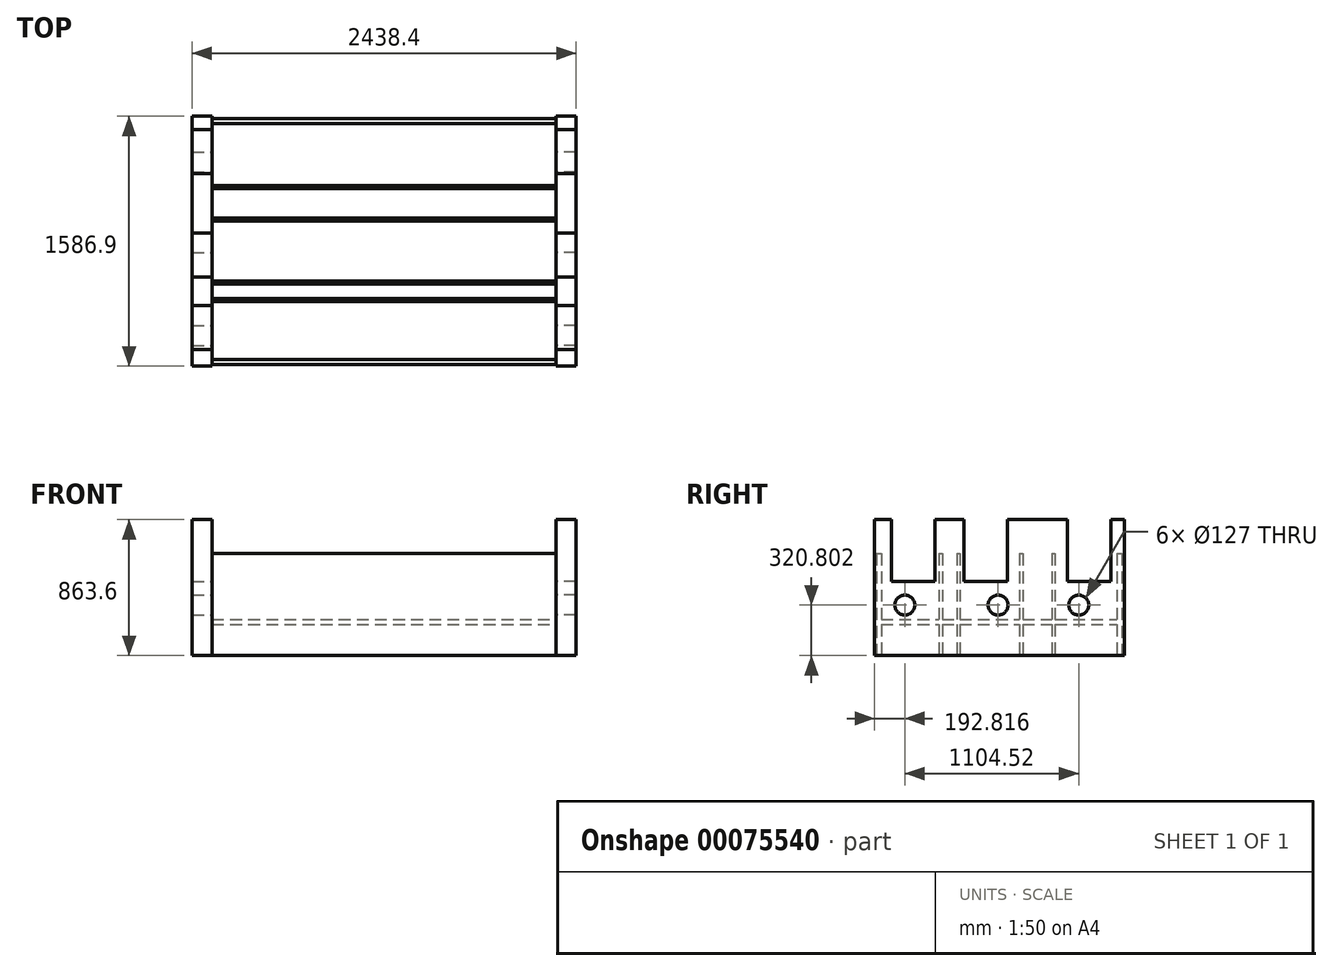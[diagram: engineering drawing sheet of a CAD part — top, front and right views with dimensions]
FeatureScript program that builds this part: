
annotation { "Feature Type Name" : "Feature", "Feature Type Description" : "" }
export const myFeature = defineFeature(function(context is Context, id is Id, definition is map)
    precondition{}
    {
        {
            var Q0;
            Q0=qCreatedBy(makeId("Right.planeOp"),FACE);
            var sketch = newSketch(context, id + "F0", { "sketchPlane" : qUnion([Q0])});
            skLineSegment(sketch, "E0", {"start": v(-793.45, 0) * mm, "end": v(793.45, 0) * mm});
            skLineSegment(sketch, "E1.0", {"start": v(-793.45, 863.6) * mm, "end": v(-686.92, 863.6) * mm});
            skLineSegment(sketch, "E2", {"start": v(-793.45, 0) * mm, "end": v(-793.45, 863.6) * mm});
            skLineSegment(sketch, "E3", {"start": v(793.45, 0) * mm, "end": v(793.45, 863.6) * mm});
            skLineSegment(sketch, "E4.0", {"start": v(-408.28, 0) * mm, "end": v(-408.28, 863.6) * mm, "construction": true});
            skLineSegment(sketch, "E5.0", {"start": v(-686.92, 0) * mm, "end": v(-686.92, 863.6) * mm, "construction": true});
            skLineSegment(sketch, "E6.0", {"start": v(52.1, 0) * mm, "end": v(52.1, 863.6) * mm, "construction": true});
            skLineSegment(sketch, "E7.0", {"start": v(-226.54, 0) * mm, "end": v(-226.54, 863.6) * mm, "construction": true});
            skLineSegment(sketch, "E8.0", {"start": v(709.12, 0) * mm, "end": v(709.12, 939.8) * mm, "construction": true});
            skLineSegment(sketch, "E9.0", {"start": v(430.48, 0) * mm, "end": v(430.48, 863.6) * mm, "construction": true});
            skLineSegment(sketch, "E10.top", {"start": v(-686.92, 469.9) * mm, "end": v(-408.28, 469.9) * mm});
            skLineSegment(sketch, "E10.left", {"start": v(-686.92, 863.6) * mm, "end": v(-686.92, 469.9) * mm});
            skLineSegment(sketch, "E10.right", {"start": v(-408.28, 863.6) * mm, "end": v(-408.28, 469.9) * mm});
            skLineSegment(sketch, "E11.top", {"start": v(-226.54, 469.9) * mm, "end": v(52.1, 469.9) * mm});
            skLineSegment(sketch, "E11.left", {"start": v(-226.54, 863.6) * mm, "end": v(-226.54, 469.9) * mm});
            skLineSegment(sketch, "E11.right", {"start": v(52.1, 863.6) * mm, "end": v(52.1, 469.9) * mm});
            skLineSegment(sketch, "E12.top", {"start": v(430.48, 469.9) * mm, "end": v(709.12, 469.9) * mm});
            skLineSegment(sketch, "E12.left", {"start": v(430.48, 863.6) * mm, "end": v(430.48, 469.9) * mm});
            skLineSegment(sketch, "E12.right", {"start": v(709.12, 863.6) * mm, "end": v(709.12, 469.9) * mm});
            skLineSegment(sketch, "E13.trimOffspring", {"start": v(-408.28, 863.6) * mm, "end": v(-226.54, 863.6) * mm});
            skLineSegment(sketch, "E14.trimOffspring", {"start": v(52.1, 863.6) * mm, "end": v(430.48, 863.6) * mm});
            skLineSegment(sketch, "E15.trimOffspring", {"start": v(709.12, 863.6) * mm, "end": v(793.45, 863.6) * mm});
            skLineSegment(sketch, "E16.0", {"start": v(503.89, -556.3) * mm, "end": v(503.89, 863.6) * mm, "construction": true});
            skLineSegment(sketch, "E17.0", {"start": v(-8.3, -556.3) * mm, "end": v(-8.3, 863.6) * mm, "construction": true});
            skLineSegment(sketch, "E18.0", {"start": v(-600.63, -556.3) * mm, "end": v(-600.63, 863.6) * mm, "construction": true});
            skLineSegment(sketch, "E19", {"start": v(793.45, 863.6) * mm, "end": v(-1048.26, 863.6) * mm, "construction": true});
            skLineSegment(sketch, "E20.0", {"start": v(793.45, 244.6) * mm, "end": v(-1048.26, 244.6) * mm, "construction": true});
            skLineSegment(sketch, "E21.0", {"start": v(793.45, 320.8) * mm, "end": v(-1048.26, 320.8) * mm, "construction": true});
            skCircle(sketch, "E22", {"center": v(-600.63, 320.8) * mm, "radius": 63.5 * mm});
            skCircle(sketch, "E23", {"center": v(-8.3, 320.8) * mm, "radius": 63.5 * mm});
            skCircle(sketch, "E24", {"center": v(503.89, 320.8) * mm, "radius": 63.5 * mm});
            skSolve(sketch);
        }
        {
            var Q0;
            Q0 = qSketchRegion(id + "F0", true);
            extrude(context, id + "F1", {"entities" : qUnion([Q0]), "depth" : 127 * mm});
        }
        {
            var Q0;
            Q0=makeQuery(id+"F0.imprint","IMPRINT",FACE,{"disambiguationData":[TD([[makeQuery(id+"F0.imprint","IMPRINT",EDGE,{"derivedFrom":sQuery(id+"F0.wireOp",EDGE,"E0")}),1.0]])]});
            var sketch = newSketch(context, id + "F2", { "sketchPlane" : qUnion([Q0])});
            skLineSegment(sketch, "E25.0", {"start": v(430.48, 469.9) * mm, "end": v(709.12, 469.9) * mm, "construction": true});
            skLineSegment(sketch, "E26.0", {"start": v(-226.54, 469.9) * mm, "end": v(52.1, 469.9) * mm, "construction": true});
            skLineSegment(sketch, "E27.0", {"start": v(-686.92, 469.9) * mm, "end": v(-408.28, 469.9) * mm, "construction": true});
            skLineSegment(sketch, "E28.0", {"start": v(709.12, 863.6) * mm, "end": v(709.12, 469.9) * mm, "construction": true});
            skLineSegment(sketch, "E29.0", {"start": v(430.48, 863.6) * mm, "end": v(430.48, 469.9) * mm, "construction": true});
            skLineSegment(sketch, "E30.0", {"start": v(709.12, 863.6) * mm, "end": v(793.45, 863.6) * mm, "construction": true});
            skLineSegment(sketch, "E31.0", {"start": v(52.1, 863.6) * mm, "end": v(430.48, 863.6) * mm, "construction": true});
            skLineSegment(sketch, "E32.0", {"start": v(52.1, 863.6) * mm, "end": v(52.1, 469.9) * mm, "construction": true});
            skLineSegment(sketch, "E33.0", {"start": v(-226.54, 863.6) * mm, "end": v(-226.54, 469.9) * mm, "construction": true});
            skLineSegment(sketch, "E34.0", {"start": v(-408.28, 863.6) * mm, "end": v(-226.54, 863.6) * mm, "construction": true});
            skLineSegment(sketch, "E35.0", {"start": v(-408.28, 863.6) * mm, "end": v(-408.28, 469.9) * mm, "construction": true});
            skLineSegment(sketch, "E36.0", {"start": v(-686.92, 863.6) * mm, "end": v(-686.92, 469.9) * mm, "construction": true});
            skLineSegment(sketch, "E37.0", {"start": v(-793.45, 863.6) * mm, "end": v(-686.92, 863.6) * mm, "construction": true});
            skLineSegment(sketch, "E38.0", {"start": v(-793.45, 0) * mm, "end": v(-793.45, 863.6) * mm, "construction": true});
            skLineSegment(sketch, "E39.0", {"start": v(-793.45, 0) * mm, "end": v(793.45, 0) * mm, "construction": true});
            skLineSegment(sketch, "E40.0", {"start": v(793.45, 0) * mm, "end": v(793.45, 863.6) * mm, "construction": true});
            skCircle(sketch, "E41.0", {"center": v(503.89, 320.8) * mm, "radius": 63.5 * mm, "construction": true});
            skCircle(sketch, "E42.0", {"center": v(-8.3, 320.8) * mm, "radius": 63.5 * mm, "construction": true});
            skCircle(sketch, "E43.0", {"center": v(-600.63, 320.8) * mm, "radius": 63.5 * mm, "construction": true});
            skLineSegment(sketch, "E44.0", {"start": v(793.45, 244.6) * mm, "end": v(-1048.26, 244.6) * mm, "construction": true});
            skLineSegment(sketch, "E45", {"start": v(569.8, 469.9) * mm, "end": v(569.8, -392.27) * mm, "construction": true});
            skLineSegment(sketch, "E46", {"start": v(-87.22, 469.9) * mm, "end": v(-87.22, -400.88) * mm, "construction": true});
            skLineSegment(sketch, "E47", {"start": v(-547.6, 469.9) * mm, "end": v(-547.6, -378.83) * mm, "construction": true});
            skLineSegment(sketch, "E48.0", {"start": v(-782.55, 647.7) * mm, "end": v(-750.8, 647.7) * mm});
            skLineSegment(sketch, "E49.0", {"start": v(-382.5, 647.7) * mm, "end": v(-382.5, 0) * mm});
            skLineSegment(sketch, "E50.0", {"start": v(-750.8, 647.7) * mm, "end": v(-750.8, 0) * mm});
            skLineSegment(sketch, "E51.0", {"start": v(-782.55, 647.7) * mm, "end": v(-782.55, 0) * mm});
            skLineSegment(sketch, "E52.0", {"start": v(-363.45, 647.7) * mm, "end": v(-363.45, 0) * mm});
            skLineSegment(sketch, "E53.0", {"start": v(128.68, 647.7) * mm, "end": v(128.68, 0) * mm});
            skLineSegment(sketch, "E54.0", {"start": v(147.73, 647.7) * mm, "end": v(147.73, 0) * mm});
            skLineSegment(sketch, "E55.0", {"start": v(-252.32, 647.7) * mm, "end": v(-252.32, 0) * mm});
            skLineSegment(sketch, "E56.0", {"start": v(-271.37, 647.7) * mm, "end": v(-271.37, 0) * mm});
            skLineSegment(sketch, "E57.0", {"start": v(747.6, 647.7) * mm, "end": v(747.6, 0) * mm});
            skLineSegment(sketch, "E58.0", {"start": v(779.35, 647.7) * mm, "end": v(779.35, 0) * mm});
            skLineSegment(sketch, "E59.0", {"start": v(353.9, 647.7) * mm, "end": v(353.9, 0) * mm});
            skLineSegment(sketch, "E60.0", {"start": v(334.85, 647.7) * mm, "end": v(334.85, 0) * mm});
            skLineSegment(sketch, "E61.trimOffspring", {"start": v(-382.5, 647.7) * mm, "end": v(-363.45, 647.7) * mm});
            skLineSegment(sketch, "E62.trimOffspring", {"start": v(128.68, 647.7) * mm, "end": v(147.73, 647.7) * mm});
            skLineSegment(sketch, "E63.trimOffspring", {"start": v(747.6, 647.7) * mm, "end": v(779.35, 647.7) * mm});
            skLineSegment(sketch, "E64.trimOffspring", {"start": v(334.85, 647.7) * mm, "end": v(430.48, 647.7) * mm});
            skLineSegment(sketch, "E65.trimOffspring", {"start": v(-271.37, 647.7) * mm, "end": v(-252.32, 647.7) * mm});
            skLineSegment(sketch, "E66", {"start": v(779.35, 0) * mm, "end": v(747.6, 0) * mm});
            skLineSegment(sketch, "E67", {"start": v(353.9, 0) * mm, "end": v(334.85, 0) * mm});
            skLineSegment(sketch, "E68", {"start": v(147.73, 0) * mm, "end": v(128.68, 0) * mm});
            skLineSegment(sketch, "E69", {"start": v(-252.32, 0) * mm, "end": v(-271.37, 0) * mm});
            skLineSegment(sketch, "E70", {"start": v(-363.45, 0) * mm, "end": v(-382.5, 0) * mm});
            skLineSegment(sketch, "E71", {"start": v(-750.8, 0) * mm, "end": v(-782.55, 0) * mm});
            skLineSegment(sketch, "E72.0", {"start": v(-793.45, 228.6) * mm, "end": v(779.35, 228.6) * mm});
            skLineSegment(sketch, "E73.0", {"start": v(-793.45, 196.85) * mm, "end": v(779.35, 196.85) * mm});
            skSolve(sketch);
        }
        {
            var Q0;
            Q0 = qSketchRegion(id + "F2", true);
            extrude(context, id + "F3", {"entities" : qUnion([Q0]), "oppositeDirection" : true, "depth" : 2184.4 * mm});
        }
        {
            var Q0;
            Q0=makeQuery(id+"F3.opExtrude","CAP_FACE",FACE,{"disambiguationData":[OSD([sQuery(id+"F2.wireOp",EDGE,"E48.0"),sQuery(id+"F2.wireOp",EDGE,"E49.0"),sQuery(id+"F2.wireOp",EDGE,"E50.0"),sQuery(id+"F2.wireOp",EDGE,"E51.0"),sQuery(id+"F2.wireOp",EDGE,"E52.0"),sQuery(id+"F2.wireOp",EDGE,"E53.0"),sQuery(id+"F2.wireOp",EDGE,"E54.0"),sQuery(id+"F2.wireOp",EDGE,"E55.0"),sQuery(id+"F2.wireOp",EDGE,"E56.0"),sQuery(id+"F2.wireOp",EDGE,"E57.0"),sQuery(id+"F2.wireOp",EDGE,"E58.0"),sQuery(id+"F2.wireOp",EDGE,"E59.0"),sQuery(id+"F2.wireOp",EDGE,"E60.0"),sQuery(id+"F2.wireOp",EDGE,"E61.trimOffspring"),sQuery(id+"F2.wireOp",EDGE,"E62.trimOffspring"),sQuery(id+"F2.wireOp",EDGE,"E63.trimOffspring"),sQuery(id+"F2.wireOp",EDGE,"E64.trimOffspring"),sQuery(id+"F2.wireOp",EDGE,"E65.trimOffspring"),sQuery(id+"F2.wireOp",EDGE,"E66"),sQuery(id+"F2.wireOp",EDGE,"E67"),sQuery(id+"F2.wireOp",EDGE,"E68"),sQuery(id+"F2.wireOp",EDGE,"E69"),sQuery(id+"F2.wireOp",EDGE,"E70"),sQuery(id+"F2.wireOp",EDGE,"E71"),sQuery(id+"F2.wireOp",EDGE,"E72.0"),sQuery(id+"F2.wireOp",EDGE,"E73.0")])],"isStart":true});
            cPlane(context, id + "F4", {"entities" : qUnion([Q0]), "cplaneType" : CPlaneType.OFFSET, "offset" : 1092.2 * mm, "oppositeDirection" : true, "width" : 152.4 * mm, "height" : 152.4 * mm});
        }
        {
            var Q0;
            Q0=makeQuery(id+"F1.opExtrude","SWEPT_BODY",BODY,{"disambiguationData":[OSD([sQuery(id+"F0.wireOp",EDGE,"E0"),sQuery(id+"F0.wireOp",EDGE,"E1.0"),sQuery(id+"F0.wireOp",EDGE,"E2"),sQuery(id+"F0.wireOp",EDGE,"E3"),sQuery(id+"F0.wireOp",EDGE,"E10.top"),sQuery(id+"F0.wireOp",EDGE,"E10.left"),sQuery(id+"F0.wireOp",EDGE,"E10.right"),sQuery(id+"F0.wireOp",EDGE,"E11.top"),sQuery(id+"F0.wireOp",EDGE,"E11.left"),sQuery(id+"F0.wireOp",EDGE,"E11.right"),sQuery(id+"F0.wireOp",EDGE,"E12.top"),sQuery(id+"F0.wireOp",EDGE,"E12.left"),sQuery(id+"F0.wireOp",EDGE,"E12.right"),sQuery(id+"F0.wireOp",EDGE,"E13.trimOffspring"),sQuery(id+"F0.wireOp",EDGE,"E14.trimOffspring"),sQuery(id+"F0.wireOp",EDGE,"E15.trimOffspring"),sQuery(id+"F0.wireOp",EDGE,"E22"),sQuery(id+"F0.wireOp",EDGE,"E23"),sQuery(id+"F0.wireOp",EDGE,"E24")])]});
            var Q1;
            Q1=qCreatedBy(id+"F4.planeOp",FACE);
            mirror(context, id + "F5", {"entities" : qUnion([Q0]), "mirrorPlane" : qUnion([Q1])});
        }
    });
